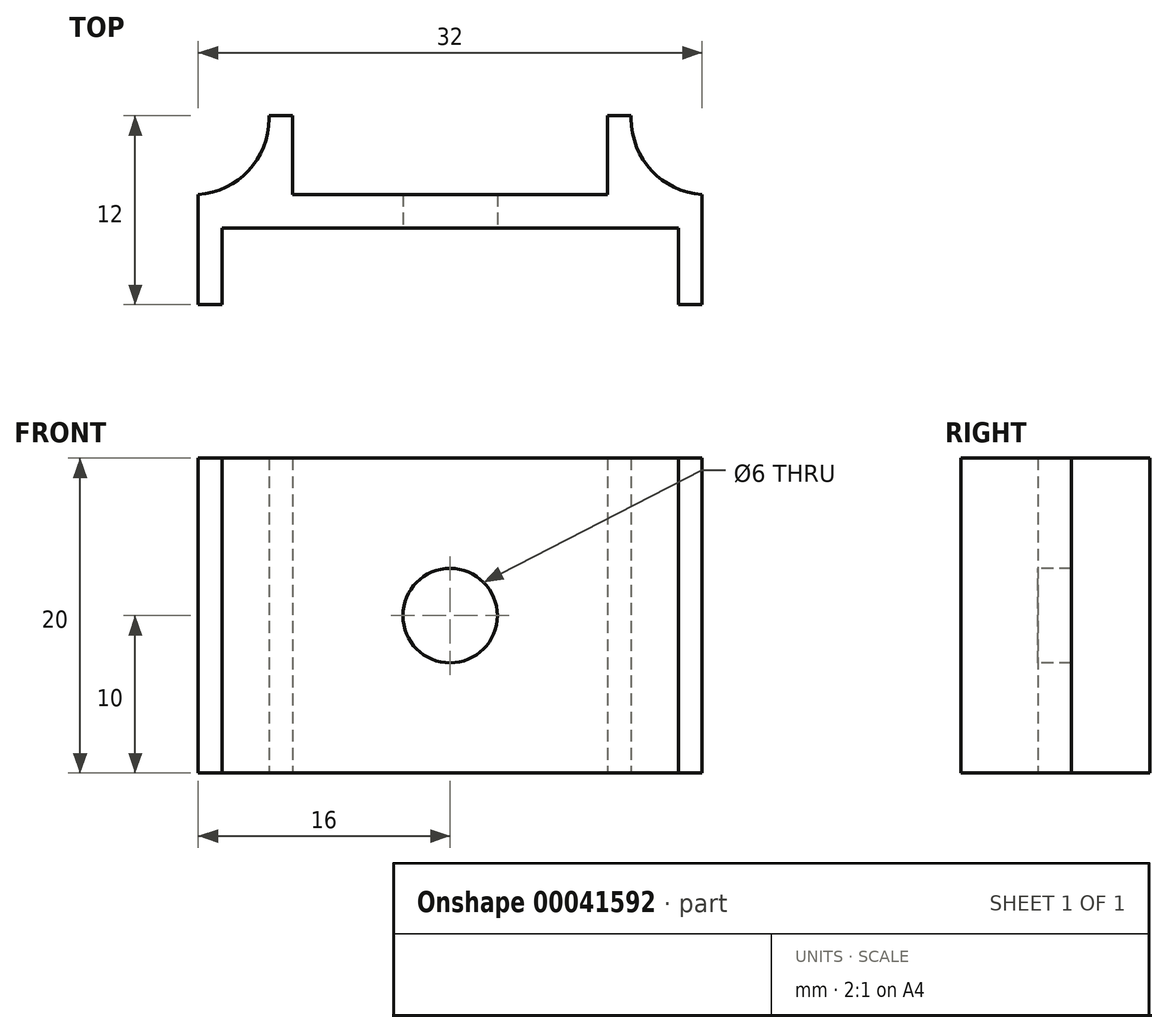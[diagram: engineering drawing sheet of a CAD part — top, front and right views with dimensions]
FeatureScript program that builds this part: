
annotation { "Feature Type Name" : "Feature", "Feature Type Description" : "" }
export const myFeature = defineFeature(function(context is Context, id is Id, definition is map)
    precondition{}
    {
        {
            var Q0;
            Q0=qCreatedBy(makeId("Top.planeOp"),FACE);
            var sketch = newSketch(context, id + "F0", { "sketchPlane" : qUnion([Q0])});
            skLineSegment(sketch, "E0", {"start": v(0, 0) * mm, "end": v(-4.5, 0) * mm});
            skLineSegment(sketch, "E1", {"start": v(-32, 0) * mm, "end": v(-32, -7) * mm});
            skLineSegment(sketch, "E2", {"start": v(-32, -7) * mm, "end": v(-30.5, -7) * mm});
            skLineSegment(sketch, "E3", {"start": v(-30.5, -7) * mm, "end": v(-30.5, -2.12) * mm});
            skLineSegment(sketch, "E4", {"start": v(-30.5, -2.12) * mm, "end": v(-1.5, -2.12) * mm});
            skLineSegment(sketch, "E5", {"start": v(-1.5, -2.12) * mm, "end": v(-1.5, -7) * mm});
            skLineSegment(sketch, "E6", {"start": v(-1.5, -7) * mm, "end": v(0, -7) * mm});
            skLineSegment(sketch, "E7", {"start": v(0, -7) * mm, "end": v(0, 0) * mm});
            skLineSegment(sketch, "E8", {"start": v(-27.5, 0) * mm, "end": v(-27.5, 5) * mm});
            skLineSegment(sketch, "E9", {"start": v(-27.5, 5) * mm, "end": v(-26, 5) * mm});
            skLineSegment(sketch, "E10", {"start": v(-26, 5) * mm, "end": v(-26, 0) * mm});
            skLineSegment(sketch, "E11", {"start": v(-4.5, 0) * mm, "end": v(-4.5, 5) * mm});
            skLineSegment(sketch, "E12", {"start": v(-6, 5) * mm, "end": v(-4.5, 5) * mm});
            skLineSegment(sketch, "E13", {"start": v(-6, 5) * mm, "end": v(-6, 0) * mm});
            skLineSegment(sketch, "E14.trimOffspring", {"start": v(-27.5, 0) * mm, "end": v(-32, 0) * mm});
            skLineSegment(sketch, "E15.trimOffspring", {"start": v(-6, 0) * mm, "end": v(-26, 0) * mm});
            skLineSegment(sketch, "E16", {"start": v(-16, -2.12) * mm, "end": v(-16, -8) * mm, "construction": true});
            skSolve(sketch);
        }
        {
            var Q0;
            Q0=makeQuery(id+"F0.imprint","IMPRINT",FACE,{"disambiguationData":[TD([[makeQuery(id+"F0.imprint","IMPRINT",EDGE,{"derivedFrom":sQuery(id+"F0.wireOp",EDGE,"E0")}),1.0]])]});
            extrude(context, id + "F1", {"entities" : qUnion([Q0]), "depth" : 20 * mm});
        }
        {
            var Q0;
            Q0=makeQuery(id+"F1.opExtrude","SWEPT_EDGE",EDGE,{"disambiguationData":[OSD([sQuery(id+"F0.wireOp",EDGE,"E8"),sQuery(id+"F0.wireOp",EDGE,"E14.trimOffspring")])]});
            var Q1;
            Q1=makeQuery(id+"F1.opExtrude","SWEPT_EDGE",EDGE,{"disambiguationData":[OSD([sQuery(id+"F0.wireOp",EDGE,"E0"),sQuery(id+"F0.wireOp",EDGE,"E11")])]});
            fillet(context, id + "F2", {"entities" : qUnion([Q0, Q1]), "radius" : 4.83 * mm, "tangentPropagation" : true, "allowEdgeOverflow" : false});
        }
        {
            var Q0;
            Q0=makeQuery(id+"F1.opExtrude","SWEPT_FACE",FACE,{"disambiguationData":[OSD([sQuery(id+"F0.wireOp",EDGE,"E4")])]});
            var sketch = newSketch(context, id + "F3", { "sketchPlane" : qUnion([Q0])});
            skLineSegment(sketch, "E17", {"start": v(-16, 20) * mm, "end": v(-16, 0) * mm, "construction": true});
            skLineSegment(sketch, "E18", {"start": v(-30.5, 10) * mm, "end": v(-1.5, 10) * mm, "construction": true});
            skCircle(sketch, "E19", {"center": v(-16, 10) * mm, "radius": 3 * mm});
            skSolve(sketch);
        }
        {
            var Q0;
            Q0=makeQuery(id+"F3.imprint","IMPRINT",FACE,{"disambiguationData":[TD([[makeQuery(id+"F3.imprint","IMPRINT",EDGE,{"derivedFrom":sQuery(id+"F3.wireOp",EDGE,"E19")}),1.0]])]});
            extrude(context, id + "F4", {"entities" : qUnion([Q0]), "operationType" : NewBodyOperationType.REMOVE, "oppositeDirection" : true, "depth" : 25 * mm});
        }
    });
